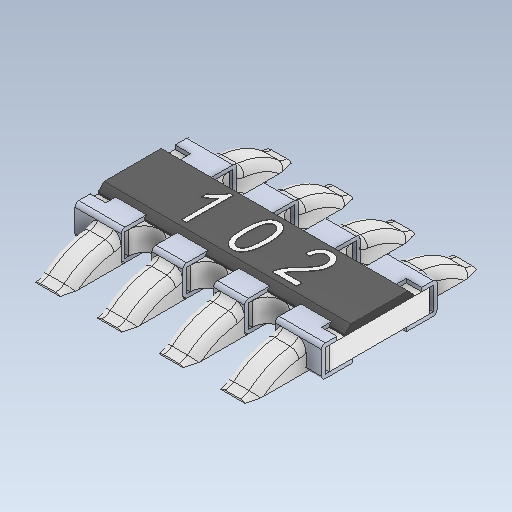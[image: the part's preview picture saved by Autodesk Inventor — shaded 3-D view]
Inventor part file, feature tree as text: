
AUTODESK INVENTOR PART (.ipt)
format: ipt  version: 2020 (Build 240168000, 168)  size: 571,904 bytes
history: native  units: in
note: dims shown in document units (in); Inventor stores cm internally (conversion verified against a paired STEP export)
features: other x8, fillet x2
ambient origin geometry x8: Origin, YZ Plane, XZ Plane, XY Plane, X Axis, Y Axis, Z Axis, Center Point
bodies: Solid1 (feature_tree), Solid2 (feature_tree), Solid3 (feature_tree), Solid4 (feature_tree), Solid5 (feature_tree), Solid6 (feature_tree), Solid7 (feature_tree), Solid8 (feature_tree), Solid9 (feature_tree), Solid10 (feature_tree)
feature tree (10):
  other  "Cut-Extrude7"
  other  "Boss-Extrude5"
  fillet  "Fillet2"  [1 undecoded]
  fillet  "Fillet1"  [1 undecoded]
  other  "LPattern3[1]"
  other  "LPattern3[2]"
  other  "LPattern3[3]"
  other  "LPattern3[4]"
  other  "LPattern3[5]"
  other  "LPattern3[6]"
note: 2 required parameter values undecoded (feature->parameter linkage not recoverable at this tier; creation-order binding heuristic only, values carry confidence <= 0.55)
